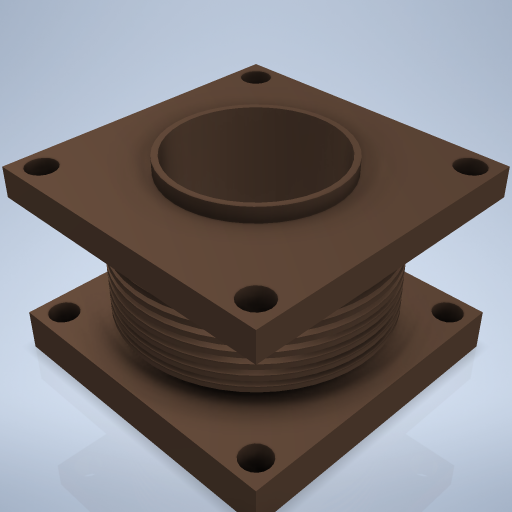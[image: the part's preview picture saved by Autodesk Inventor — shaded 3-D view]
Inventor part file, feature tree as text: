
AUTODESK INVENTOR PART (.ipt)
format: ipt  version: 2024.2 (Build 282272000, 272)  size: 408,576 bytes
history: native  units: mm
features: sketch x7, plane x4, hole x3, revolve x2, extrude x2, projected_geometry x1
ambient origin geometry x8: Origin, YZ Plane, XZ Plane, XY Plane, X Axis, Y Axis, Z Axis, Center Point
bodies: Volumenkörper1 (feature_tree)
feature tree (19):
  revolve  "Umdrehung1"
  plane  "Arbeitsebene1"
  plane  "Arbeitsebene2"
  extrude  "Extrusion1"  Depth=35.5mm
  plane  "Arbeitsebene3"
  revolve  "Umdrehung2"
  plane  "Arbeitsebene4"
  extrude  "Extrusion2"  TaperAngle=0.0deg  [1 undecoded]
  hole  "Bohrung1"  [1 undecoded]
  hole  "Bohrung2"  [1 undecoded]
  hole  "Bohrung3"  [1 undecoded]
  sketch  "Skizze2"  dims[d2=29.0mm d3=35.5mm]
  sketch  "Skizze4"  dims[d4=90.0deg d5=0.0mm d6=-2.5mm]
  sketch  "Skizze5"  dims[d7=50.0mm d8=50.0mm]
  projected_geometry  "Projizierte Kontur3"
  sketch  "Skizze6"  dims[d9=5.0mm d10=0.0mm d11=0.0mm]
  sketch  "Skizze7"  dims[d12=1.0mm d13=2.0mm]
  sketch  "Skizze8"  dims[d14=44.0mm]
  sketch  "Skizze9"  dims[d15=1.0mm d16=1.0mm d17=1.0mm d18=1.0mm d19=1.0mm d20=1.0mm d21=1.0mm d22=1.0mm d23=1.0mm d24=1.0mm d25=1.0mm d26=1.0mm d27=1.0mm d28=1.0mm d29=44.0mm d30=90.0deg d31=0.0mm d32=50.0mm d33=50.0mm d34=7.0mm d35=0.0mm d36=27.0mm d37=6.0mm d38=4.0mm d39=2.0mm d40=90.0deg d41=8.0mm d42=20.594885mm d43=5.0mm d44=6.0mm d45=4.0mm d46=2.0mm d47=90.0deg d48=8.0mm d49=20.594885mm d58=5.0mm d59=6.0mm d60=4.0mm d61=2.0mm d62=90.0deg d63=8.0mm d64=20.594885mm d73=42.248mm d74=42.248mm d75=42.248mm d76=42.248mm]
note: 4 required parameter values undecoded (feature->parameter linkage not recoverable at this tier; creation-order binding heuristic only, values carry confidence <= 0.55)
